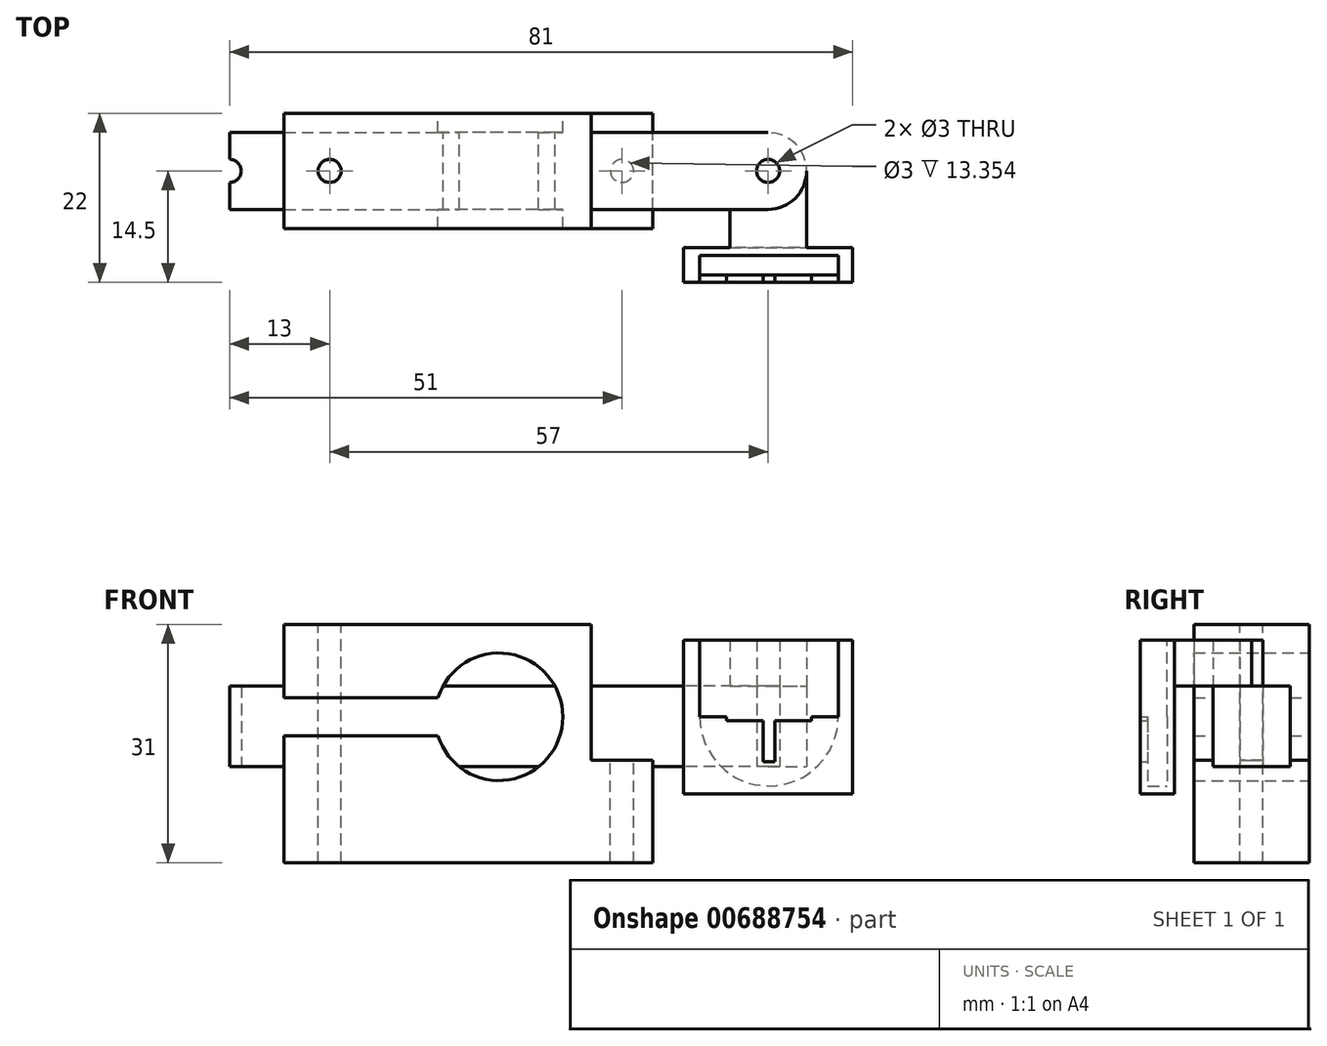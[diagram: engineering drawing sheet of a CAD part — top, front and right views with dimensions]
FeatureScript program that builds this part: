
annotation { "Feature Type Name" : "Feature", "Feature Type Description" : "" }
export const myFeature = defineFeature(function(context is Context, id is Id, definition is map)
    precondition{}
    {
        {
            var Q0;
            Q0=qCreatedBy(makeId("Top.planeOp"),FACE);
            var sketch = newSketch(context, id + "F0", { "sketchPlane" : qUnion([Q0])});
            skCircle(sketch, "E0", {"center": v(0, 0) * mm, "radius": 1.5 * mm});
            skCircle(sketch, "E1", {"center": v(0, 0) * mm, "radius": 3 * mm});
            skSolve(sketch);
        }
        {
            var Q0;
            Q0=qSketchRegion(id+"F0",true);
            extrude(context, id + "F1", {"entities" : qUnion([Q0]), "depth" : 4 * mm, "offsetDistance" : 25 * mm});
        }
        {
            var Q0;
            Q0=qCreatedBy(makeId("Top.planeOp"),FACE);
            var sketch = newSketch(context, id + "F2", { "sketchPlane" : qUnion([Q0])});
            skLineSegment(sketch, "E2.bottom", {"start": v(35, 5) * mm, "end": v(-35, 5) * mm});
            skLineSegment(sketch, "E2.top", {"start": v(35, -5) * mm, "end": v(-35, -5) * mm});
            skLineSegment(sketch, "E2.left", {"start": v(35, 5) * mm, "end": v(35, -5) * mm});
            skLineSegment(sketch, "E2.right", {"start": v(-35, 5) * mm, "end": v(-35, -5) * mm});
            skPoint(sketch, "E2.middle", {"position": v(0, 0) * mm});
            skArc(sketch, "E3", {"start": v(35, -5) * mm, "mid": v(40, 0) * mm, "end": v(35, 5) * mm});
            skLineSegment(sketch, "E4", {"start": v(0, 15.84) * mm, "end": v(0, -21.96) * mm, "construction": true});
            skPoint(sketch, "E4.startSnap0", {"position": v(0, 5) * mm});
            skPoint(sketch, "E4.endSnap0", {"position": v(0, -5) * mm});
            skArc(sketch, "E5.MirrorCS", {"start": v(-35, -5) * mm, "mid": v(-40, 0) * mm, "end": v(-35, 5) * mm});
            skCircle(sketch, "E6", {"center": v(-35, 0) * mm, "radius": 1.5 * mm});
            skCircle(sketch, "E7.MirrorC", {"center": v(35, 0) * mm, "radius": 1.5 * mm});
            skSolve(sketch);
        }
        {
            var Q0;
            {var subQ5=sQuery(id+"F2.wireOp",EDGE,"E2.bottom");Q0=makeQuery(id+"F2.imprint","IMPRINT",FACE,{"disambiguationData":[TD([[makeQuery(id+"F2.imprint","IMPRINT",EDGE,{"derivedFrom":subQ5}),1.0]])]});}
            var Q1;
            {var subQ0=sQuery(id+"F2.wireOp",EDGE,"E5.MirrorCS");Q1=makeQuery(id+"F2.imprint","IMPRINT",FACE,{"disambiguationData":[TD([[makeQuery(id+"F2.imprint","IMPRINT",EDGE,{"derivedFrom":subQ0}),-1.0]])]});}
            var Q2;
            {var subQ0=sQuery(id+"F2.wireOp",EDGE,"E3");Q2=makeQuery(id+"F2.imprint","IMPRINT",FACE,{"disambiguationData":[TD([[makeQuery(id+"F2.imprint","IMPRINT",EDGE,{"derivedFrom":subQ0}),1.0]])]});}
            extrude(context, id + "F3", {"entities" : qUnion([Q0, Q1, Q2]), "depth" : 4 * mm, "offsetDistance" : 25 * mm});
        }
        {
            var Q0;
            Q0=makeQuery(id+"F3.opExtrude","CAP_FACE",FACE,{"disambiguationData":[OSD([sQuery(id+"F2.wireOp",EDGE,"E2.bottom"),sQuery(id+"F2.wireOp",EDGE,"E2.top"),sQuery(id+"F2.wireOp",EDGE,"E3"),sQuery(id+"F2.wireOp",EDGE,"E5.MirrorCS"),sQuery(id+"F2.wireOp",EDGE,"E6"),sQuery(id+"F2.wireOp",EDGE,"E7.MirrorC")])],"isStart":false});
            var sketch = newSketch(context, id + "F4", { "sketchPlane" : qUnion([Q0])});
            skCircle(sketch, "E8", {"center": v(35, 0) * mm, "radius": 1.5 * mm});
            skArc(sketch, "E9", {"start": v(40, 0) * mm, "mid": v(35, 5) * mm, "end": v(30, 0) * mm});
            skPoint(sketch, "E9.endSnap0", {"position": v(40, 0) * mm});
            skLineSegment(sketch, "E10.bottom", {"start": v(30, 0) * mm, "end": v(40, 0) * mm});
            skLineSegment(sketch, "E10.top", {"start": v(30, -10) * mm, "end": v(40, -10) * mm});
            skLineSegment(sketch, "E10.left", {"start": v(30, 0) * mm, "end": v(30, -10) * mm});
            skLineSegment(sketch, "E10.right", {"start": v(40, 0) * mm, "end": v(40, -10) * mm});
            skSolve(sketch);
        }
        {
            var Q0;
            {var subQ0=sQuery(id+"F4.wireOp",EDGE,"E10.bottom");var subQ3=sQuery(id+"F4.wireOp",EDGE,"E8");var subQ4=makeQuery(id+"F4.imprint","INTERSECT",VERTEX,{"disambiguationData":[OD(0.0)],"derivedFrom":[subQ3,subQ0]});Q0=makeQuery(id+"F4.imprint","IMPRINT",FACE,{"disambiguationData":[TD([[makeQuery(id+"F4.imprint","IMPRINT",EDGE,{"disambiguationData":[TD([[subQ4,-1.0]])],"derivedFrom":subQ3}),1.0]])]});}
            var Q1;
            {var subQ1=sQuery(id+"F4.wireOp",EDGE,"E10.bottom");var subQ6=sQuery(id+"F4.wireOp",EDGE,"E8");var subQ7=makeQuery(id+"F4.imprint","INTERSECT",VERTEX,{"disambiguationData":[OD(0.0)],"derivedFrom":[subQ6,subQ1]});Q1=makeQuery(id+"F4.imprint","IMPRINT",FACE,{"disambiguationData":[TD([[makeQuery(id+"F4.imprint","IMPRINT",EDGE,{"disambiguationData":[TD([[subQ7,1.0]])],"derivedFrom":subQ6}),1.0]])]});}
            var Q2;
            {var subQ2=sQuery(id+"F4.wireOp",EDGE,"E10.top");Q2=makeQuery(id+"F4.imprint","IMPRINT",FACE,{"disambiguationData":[TD([[makeQuery(id+"F4.imprint","IMPRINT",EDGE,{"derivedFrom":subQ2}),1.0]])]});}
            extrude(context, id + "F5", {"entities" : qUnion([Q0, Q1, Q2]), "depth" : 6 * mm, "offsetDistance" : 25 * mm});
        }
        {
            var Q0;
            Q0=makeQuery(id+"F5.opExtrude","SWEPT_FACE",FACE,{"disambiguationData":[OSD([sQuery(id+"F4.wireOp",EDGE,"E10.top")])]});
            var sketch = newSketch(context, id + "F6", { "sketchPlane" : qUnion([Q0])});
            skLineSegment(sketch, "E11.bottom", {"start": v(46, -10) * mm, "end": v(24, -10) * mm});
            skLineSegment(sketch, "E11.top", {"start": v(46, 10) * mm, "end": v(24, 10) * mm});
            skLineSegment(sketch, "E11.left", {"start": v(46, -10) * mm, "end": v(46, 10) * mm});
            skLineSegment(sketch, "E11.right", {"start": v(24, -10) * mm, "end": v(24, 10) * mm});
            skPoint(sketch, "E12", {"position": v(35, -10) * mm});
            skPoint(sketch, "E13", {"position": v(40, 10) * mm});
            skPoint(sketch, "E14", {"position": v(30, 10) * mm});
            skCircle(sketch, "E15", {"center": v(35.12, 0) * mm, "radius": 9 * mm});
            skLineSegment(sketch, "E16", {"start": v(26.12, 0) * mm, "end": v(26.12, 10) * mm});
            skPoint(sketch, "E16.startSnap0", {"position": v(24.12, 0) * mm});
            skLineSegment(sketch, "E17", {"start": v(44.12, 0) * mm, "end": v(44.12, 10) * mm});
            skPoint(sketch, "E17.startSnap0", {"position": v(46.12, 0) * mm});
            skPoint(sketch, "E18", {"position": v(35.12, 9) * mm});
            skSolve(sketch);
        }
        {
            var Q0;
            {var subQ3=sQuery(id+"F6.wireOp",EDGE,"E17");Q0=makeQuery(id+"F6.imprint","IMPRINT",FACE,{"disambiguationData":[TD([[makeQuery(id+"F6.imprint","IMPRINT",EDGE,{"derivedFrom":subQ3}),1.0]])]});}
            var Q1;
            {var subQ3=sQuery(id+"F6.wireOp",EDGE,"E16");Q1=makeQuery(id+"F6.imprint","IMPRINT",FACE,{"disambiguationData":[TD([[makeQuery(id+"F6.imprint","IMPRINT",EDGE,{"derivedFrom":subQ3}),-1.0]])]});}
            var Q2;
            {var subQ0=sQuery(id+"F6.wireOp",EDGE,"E11.top");var subQ1=sQuery(id+"F4.wireOp",EDGE,"E10.top");var subQ2=makeQuery(id+"F5.opExtrude","SWEPT_EDGE",EDGE,{"disambiguationData":[OSD([subQ1,sQuery(id+"F4.wireOp",EDGE,"E10.left")])]});var subQ3=makeQuery(id+"F6.imprint","INTERSECT",VERTEX,{"derivedFrom":[subQ2,subQ0]});var subQ4=makeQuery(id+"F5.opExtrude","SWEPT_EDGE",EDGE,{"disambiguationData":[OSD([subQ1,sQuery(id+"F4.wireOp",EDGE,"E10.right")])]});var subQ5=makeQuery(id+"F6.imprint","INTERSECT",VERTEX,{"derivedFrom":[subQ4,subQ0]});Q2=makeQuery(id+"F6.imprint","IMPRINT",FACE,{"disambiguationData":[TD([[makeQuery(id+"F6.imprint","IMPRINT",EDGE,{"disambiguationData":[TD([[subQ3,-1.0],[subQ5,1.0]])],"derivedFrom":subQ0}),-1.0]])]});}
            var Q3;
            {var subQ1=sQuery(id+"F4.wireOp",EDGE,"E10.top");var subQ6=makeQuery(id+"F5.opExtrude","CAP_EDGE",EDGE,{"disambiguationData":[OSD([subQ1])],"isStart":true});Q3=makeQuery(id+"F6.imprint","IMPRINT",FACE,{"disambiguationData":[TD([[makeQuery(id+"F6.imprint","IMPRINT",EDGE,{"derivedFrom":subQ6}),1.0]])]});}
            var Q4;
            {var subQ0=sQuery(id+"F4.wireOp",EDGE,"E10.top");var subQ1=makeQuery(id+"F5.opExtrude","CAP_EDGE",EDGE,{"disambiguationData":[OSD([subQ0])],"isStart":true});Q4=makeQuery(id+"F6.imprint","IMPRINT",FACE,{"disambiguationData":[TD([[makeQuery(id+"F6.imprint","IMPRINT",EDGE,{"derivedFrom":subQ1}),-1.0]])]});}
            extrude(context, id + "F7", {"entities" : qUnion([Q0, Q1, Q2, Q3, Q4]), "operationType" : NewBodyOperationType.ADD, "depth" : 1 * mm, "offsetDistance" : 25 * mm});
        }
        {
            var Q0;
            Q0=makeQuery(id+"F6.imprint","IMPRINT",FACE,{"disambiguationData":[TD([[makeQuery(id+"F6.imprint","IMPRINT",EDGE,{"derivedFrom":sQuery(id+"F6.wireOp",EDGE,"E11.bottom")}),-1.0]])]});
            extrude(context, id + "F8", {"entities" : qUnion([Q0]), "operationType" : NewBodyOperationType.ADD, "depth" : 3.5 * mm, "offsetDistance" : 25 * mm});
        }
        {
            var Q0;
            Q0=makeQuery(id+"F8.opExtrude","CAP_FACE",FACE,{"disambiguationData":[OSD([sQuery(id+"F6.wireOp",EDGE,"E11.bottom"),sQuery(id+"F6.wireOp",EDGE,"E11.top"),sQuery(id+"F6.wireOp",EDGE,"E11.left"),sQuery(id+"F6.wireOp",EDGE,"E11.right"),sQuery(id+"F6.wireOp",EDGE,"E15"),sQuery(id+"F6.wireOp",EDGE,"E16"),sQuery(id+"F6.wireOp",EDGE,"E17")])],"isStart":false});
            var sketch = newSketch(context, id + "F9", { "sketchPlane" : qUnion([Q0])});
            skLineSegment(sketch, "E19", {"start": v(26.12, 0) * mm, "end": v(44.12, 0) * mm, "construction": true});
            skLineSegment(sketch, "E20", {"start": v(35.12, -9) * mm, "end": v(35.12, -5.85) * mm, "construction": true});
            skLineSegment(sketch, "E21", {"start": v(34.37, -5.85) * mm, "end": v(35.87, -5.85) * mm});
            skLineSegment(sketch, "E22", {"start": v(34.37, -5.85) * mm, "end": v(34.37, 5.25) * mm});
            skLineSegment(sketch, "E23", {"start": v(34.37, 5.25) * mm, "end": v(35.87, 5.25) * mm});
            skLineSegment(sketch, "E24", {"start": v(35.87, 5.25) * mm, "end": v(35.87, -5.85) * mm});
            skLineSegment(sketch, "E25.bottom", {"start": v(40.67, -0.5) * mm, "end": v(29.57, -0.5) * mm});
            skLineSegment(sketch, "E25.top", {"start": v(40.67, 0.5) * mm, "end": v(29.57, 0.5) * mm});
            skLineSegment(sketch, "E25.left", {"start": v(40.67, -0.5) * mm, "end": v(40.67, 0.5) * mm});
            skLineSegment(sketch, "E25.right", {"start": v(29.57, -0.5) * mm, "end": v(29.57, 0.5) * mm});
            skPoint(sketch, "E25.middle", {"position": v(35.12, 0) * mm});
            skLineSegment(sketch, "E26", {"start": v(26.12, 0) * mm, "end": v(44.12, 0) * mm});
            skSolve(sketch);
        }
        {
            var Q0;
            {var subQ1=sQuery(id+"F9.wireOp",EDGE,"E21");Q0=makeQuery(id+"F9.imprint","IMPRINT",FACE,{"disambiguationData":[TD([[makeQuery(id+"F9.imprint","IMPRINT",EDGE,{"derivedFrom":subQ1}),-1.0]])]});}
            var Q1;
            Q1=makeQuery(id+"F9.imprint","IMPRINT",FACE,{"disambiguationData":[TD([[makeQuery(id+"F9.imprint","IMPRINT",EDGE,{"derivedFrom":makeQuery(id+"F8.opExtrude","CAP_EDGE",EDGE,{"disambiguationData":[OSD([sQuery(id+"F6.wireOp",EDGE,"E11.bottom")])],"isStart":false})}),-1.0]])]});
            extrude(context, id + "F10", {"entities" : qUnion([Q0, Q1]), "operationType" : NewBodyOperationType.ADD, "depth" : 1 * mm, "offsetDistance" : 25 * mm});
        }
        {
            var Q0;
            Q0=makeQuery(id+"F3.opExtrude","CAP_FACE",FACE,{"disambiguationData":[OSD([sQuery(id+"F2.wireOp",EDGE,"E2.bottom"),sQuery(id+"F2.wireOp",EDGE,"E2.top"),sQuery(id+"F2.wireOp",EDGE,"E3"),sQuery(id+"F2.wireOp",EDGE,"E5.MirrorCS"),sQuery(id+"F2.wireOp",EDGE,"E6"),sQuery(id+"F2.wireOp",EDGE,"E7.MirrorC")])],"isStart":true});
            extrude(context, id + "F11", {"entities" : qUnion([Q0]), "operationType" : NewBodyOperationType.ADD, "depth" : 6.5 * mm, "offsetDistance" : 25 * mm});
        }
        {
            var Q0;
            Q0=qCreatedBy(makeId("Front.planeOp"),FACE);
            var sketch = newSketch(context, id + "F12", { "sketchPlane" : qUnion([Q0])});
            skArc(sketch, "E27", {"start": v(-7.91, -2.5) * mm, "mid": v(8.3, 0) * mm, "end": v(-7.91, 2.5) * mm});
            skLineSegment(sketch, "E28", {"start": v(0, 12) * mm, "end": v(12, 12) * mm});
            skLineSegment(sketch, "E29", {"start": v(12, 12) * mm, "end": v(12, 0) * mm});
            skLineSegment(sketch, "E30", {"start": v(12, 0) * mm, "end": v(12, -12) * mm});
            skLineSegment(sketch, "E31", {"start": v(12, -12) * mm, "end": v(0, -12) * mm});
            skLineSegment(sketch, "E32", {"start": v(0, -12) * mm, "end": v(-27.91, -12) * mm});
            skLineSegment(sketch, "E33", {"start": v(0, 12) * mm, "end": v(-27.91, 12) * mm});
            skLineSegment(sketch, "E34", {"start": v(-27.91, 12) * mm, "end": v(-27.91, 2.5) * mm});
            skLineSegment(sketch, "E35", {"start": v(-7.91, 2.5) * mm, "end": v(-27.91, 2.5) * mm});
            skLineSegment(sketch, "E36", {"start": v(-7.91, -2.5) * mm, "end": v(-27.91, -2.5) * mm});
            skLineSegment(sketch, "E37.trimOffspring", {"start": v(-27.91, -2.5) * mm, "end": v(-27.91, -12) * mm});
            skSolve(sketch);
        }
        {
            var Q0;
            Q0=makeQuery(id+"F12.imprint","IMPRINT",FACE,{"disambiguationData":[TD([[makeQuery(id+"F12.imprint","IMPRINT",EDGE,{"derivedFrom":sQuery(id+"F12.wireOp",EDGE,"E27")}),-1.0]])]});
            extrude(context, id + "F13", {"entities" : qUnion([Q0]), "depth" : 15 * mm, "offsetDistance" : 25 * mm, "symmetric" : true});
        }
        {
            var Q0;
            Q0=makeQuery(id+"F13.opExtrude","SWEPT_FACE",FACE,{"disambiguationData":[OSD([sQuery(id+"F12.wireOp",EDGE,"E28"),sQuery(id+"F12.wireOp",EDGE,"E33")])]});
            var sketch = newSketch(context, id + "F14", { "sketchPlane" : qUnion([Q0])});
            skCircle(sketch, "E38", {"center": v(-22, 0) * mm, "radius": 1.5 * mm});
            skSolve(sketch);
        }
        {
            var Q0;
            Q0=makeQuery(id+"F14.imprint","IMPRINT",FACE,{"disambiguationData":[TD([[makeQuery(id+"F14.imprint","IMPRINT",EDGE,{"derivedFrom":sQuery(id+"F14.wireOp",EDGE,"E38")}),1.0]])]});
            extrude(context, id + "F15", {"entities" : qUnion([Q0]), "operationType" : NewBodyOperationType.REMOVE, "oppositeDirection" : true, "depth" : 31.6 * mm, "offsetDistance" : 25 * mm});
        }
        {
            var Q0;
            Q0=makeQuery(id+"F13.opExtrude","SWEPT_FACE",FACE,{"disambiguationData":[OSD([sQuery(id+"F12.wireOp",EDGE,"E29"),sQuery(id+"F12.wireOp",EDGE,"E30")])]});
            var sketch = newSketch(context, id + "F16", { "sketchPlane" : qUnion([Q0])});
            skLineSegment(sketch, "E39", {"start": v(-7.5, -5.65) * mm, "end": v(7.5, -5.65) * mm});
            skLineSegment(sketch, "E40", {"start": v(7.5, -5.65) * mm, "end": v(7.5, -12) * mm});
            skLineSegment(sketch, "E41", {"start": v(7.5, -12) * mm, "end": v(-7.5, -12) * mm});
            skLineSegment(sketch, "E42", {"start": v(-7.5, -12) * mm, "end": v(-7.5, -5.65) * mm});
            skSolve(sketch);
        }
        {
            var Q0;
            Q0=makeQuery(id+"F16.imprint","IMPRINT",FACE,{"disambiguationData":[TD([[makeQuery(id+"F16.imprint","IMPRINT",EDGE,{"derivedFrom":sQuery(id+"F16.wireOp",EDGE,"E39")}),-1.0]])]});
            extrude(context, id + "F17", {"entities" : qUnion([Q0]), "operationType" : NewBodyOperationType.ADD, "depth" : 8 * mm, "offsetDistance" : 25 * mm});
        }
        {
            var Q0;
            Q0=makeQuery(id+"F17.opExtrude","SWEPT_FACE",FACE,{"disambiguationData":[OSD([sQuery(id+"F16.wireOp",EDGE,"E39")])]});
            var sketch = newSketch(context, id + "F18", { "sketchPlane" : qUnion([Q0])});
            skCircle(sketch, "E43", {"center": v(16, 0) * mm, "radius": 1.5 * mm});
            skSolve(sketch);
        }
        {
            var Q0;
            Q0=makeQuery(id+"F18.imprint","IMPRINT",FACE,{"disambiguationData":[TD([[makeQuery(id+"F18.imprint","IMPRINT",EDGE,{"derivedFrom":sQuery(id+"F18.wireOp",EDGE,"E43")}),1.0]])]});
            extrude(context, id + "F19", {"entities" : qUnion([Q0]), "operationType" : NewBodyOperationType.REMOVE, "oppositeDirection" : true, "depth" : 25 * mm, "offsetDistance" : 25 * mm});
        }
        {
            var Q0;
            Q0=makeQuery(id+"F17.boolean.opBoolean","MERGE",FACE,{"derivedFrom":[makeQuery(id+"F13.opExtrude","SWEPT_FACE",FACE,{"disambiguationData":[OSD([sQuery(id+"F12.wireOp",EDGE,"E31"),sQuery(id+"F12.wireOp",EDGE,"E32")])]}),makeQuery(id+"F17.opExtrude","SWEPT_FACE",FACE,{"disambiguationData":[OSD([sQuery(id+"F16.wireOp",EDGE,"E41")])]})]});
            extrude(context, id + "F20", {"entities" : qUnion([Q0]), "operationType" : NewBodyOperationType.ADD, "depth" : 7 * mm, "offsetDistance" : 25 * mm});
        }
    });
